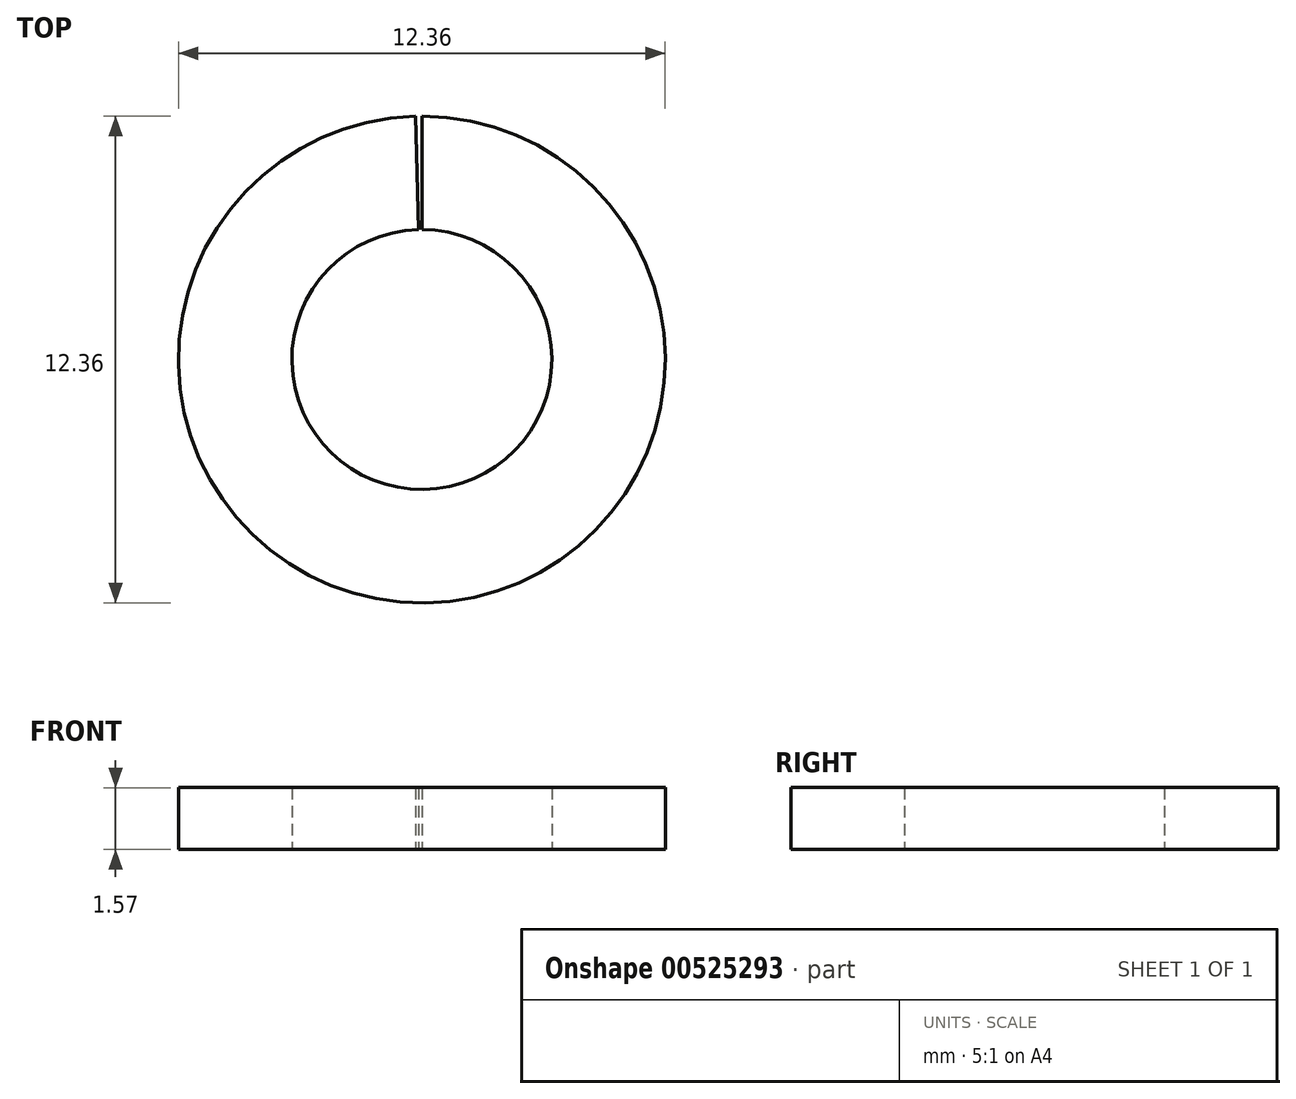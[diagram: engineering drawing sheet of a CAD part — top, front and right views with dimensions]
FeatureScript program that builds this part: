
annotation { "Feature Type Name" : "Feature", "Feature Type Description" : "" }
export const myFeature = defineFeature(function(context is Context, id is Id, definition is map)
    precondition{}
    {
        {
            var Q0;
            Q0=qCreatedBy(makeId("Top.planeOp"),FACE);
            var sketch = newSketch(context, id + "F0", { "sketchPlane" : qUnion([Q0])});
            skArc(sketch, "E0", {"start": v(-0.16, 6.18) * mm, "mid": v(0.08, -6.18) * mm, "end": v(0, 6.18) * mm});
            skArc(sketch, "E1", {"start": v(-0.09, 3.3) * mm, "mid": v(0.04, -3.3) * mm, "end": v(0, 3.3) * mm});
            skLineSegment(sketch, "E2", {"start": v(-0.09, 3.3) * mm, "end": v(-0.16, 6.18) * mm});
            skLineSegment(sketch, "E3", {"start": v(0, 3.3) * mm, "end": v(0, 6.18) * mm});
            skSolve(sketch);
        }
        {
            var Q0;
            Q0 = qSketchRegion(id + "F0", true);
            extrude(context, id + "F1", {"entities" : qUnion([Q0]), "depth" : 1.57 * mm, "offsetDistance" : 25.4 * mm});
        }
    });
